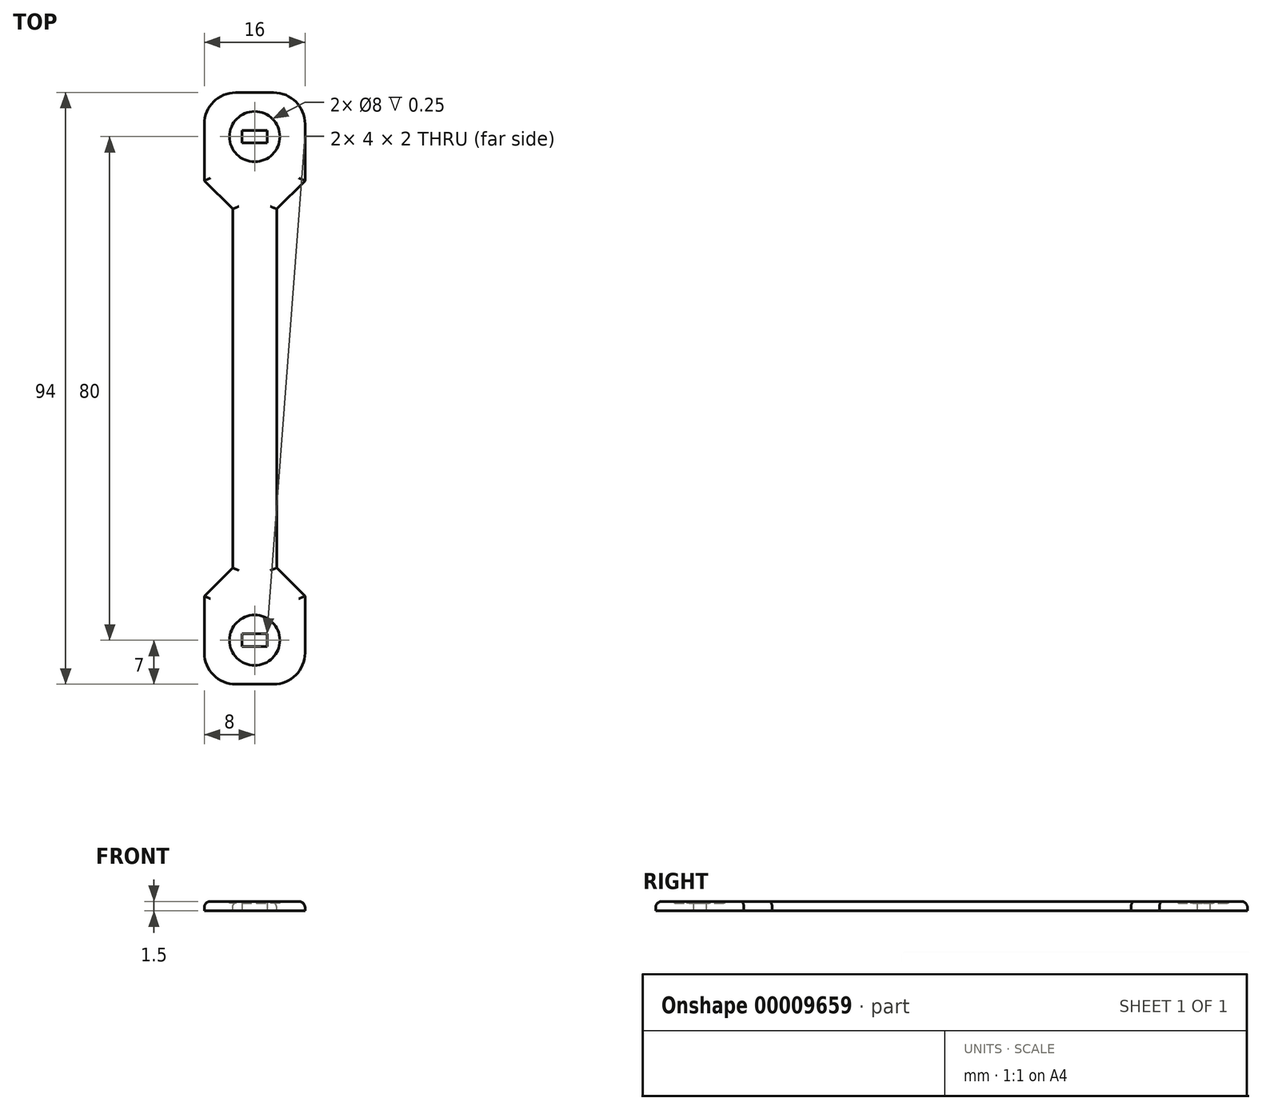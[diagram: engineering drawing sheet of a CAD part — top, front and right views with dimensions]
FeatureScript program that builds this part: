
annotation { "Feature Type Name" : "Feature", "Feature Type Description" : "" }
export const myFeature = defineFeature(function(context is Context, id is Id, definition is map)
    precondition{}
    {
        {
            var Q0;
            Q0=qCreatedBy(makeId("Top.planeOp"),FACE);
            var sketch = newSketch(context, id + "F0", { "sketchPlane" : qUnion([Q0])});
            skCircle(sketch, "E0", {"center": v(0, 40) * mm, "radius": 2 * mm, "construction": true});
            skCircle(sketch, "E1.0.MirrorC", {"center": v(0, -40) * mm, "radius": 2 * mm, "construction": true});
            skLineSegment(sketch, "E2.rect.bottom", {"start": v(-8, 47) * mm, "end": v(8, 47) * mm});
            skLineSegment(sketch, "E2.rect.top", {"start": v(-8, -47) * mm, "end": v(8, -47) * mm});
            skLineSegment(sketch, "E2.rect.left", {"start": v(-8, 47) * mm, "end": v(-8, -47) * mm});
            skLineSegment(sketch, "E2.rect.right", {"start": v(8, 47) * mm, "end": v(8, -47) * mm});
            skPoint(sketch, "E2.rect.middle", {"position": v(0, 0) * mm});
            skLineSegment(sketch, "E3", {"start": v(-8, 33) * mm, "end": v(-3.5, 33) * mm});
            skLineSegment(sketch, "E4", {"start": v(-3.5, 33) * mm, "end": v(-3.5, -33) * mm});
            skLineSegment(sketch, "E5", {"start": v(-8, 0) * mm, "end": v(-3.5, 0) * mm, "construction": true});
            skLineSegment(sketch, "E6.0.MirrorCS", {"start": v(-8, -33) * mm, "end": v(-3.5, -33) * mm});
            skLineSegment(sketch, "E7.0.MirrorCS", {"start": v(8, 33) * mm, "end": v(3.5, 33) * mm});
            skLineSegment(sketch, "E8.0.MirrorCS", {"start": v(3.5, 33) * mm, "end": v(3.5, -33) * mm});
            skLineSegment(sketch, "E9.0.MirrorCS", {"start": v(8, -33) * mm, "end": v(3.5, -33) * mm});
            skLineSegment(sketch, "E10.rect.bottom", {"start": v(-2, -41) * mm, "end": v(2, -41) * mm});
            skLineSegment(sketch, "E10.rect.top", {"start": v(-2, -39) * mm, "end": v(2, -39) * mm});
            skLineSegment(sketch, "E10.rect.left", {"start": v(-2, -41) * mm, "end": v(-2, -39) * mm});
            skLineSegment(sketch, "E10.rect.right", {"start": v(2, -41) * mm, "end": v(2, -39) * mm});
            skLineSegment(sketch, "E11.MirrorCS", {"start": v(-2, 41) * mm, "end": v(-2, 39) * mm});
            skLineSegment(sketch, "E12.MirrorCS", {"start": v(-2, 39) * mm, "end": v(2, 39) * mm});
            skLineSegment(sketch, "E13.MirrorCS", {"start": v(-2, 41) * mm, "end": v(2, 41) * mm});
            skLineSegment(sketch, "E14.MirrorCS", {"start": v(2, 41) * mm, "end": v(2, 39) * mm});
            skSolve(sketch);
        }
        {
            var Q0;
            {var subQ5=sQuery(id+"F0.wireOp",EDGE,"E2.rect.bottom");Q0=makeQuery(id+"F0.imprint","IMPRINT",FACE,{"disambiguationData":[TD([[makeQuery(id+"F0.imprint","IMPRINT",EDGE,{"derivedFrom":subQ5}),-1.0]])]});}
            extrude(context, id + "F1", {"entities" : qUnion([Q0]), "depth" : 1.5 * mm});
        }
        {
            var Q0;
            Q0=makeQuery(id+"F1.opExtrude","SWEPT_EDGE",EDGE,{"disambiguationData":[OSD([sQuery(id+"F0.wireOp",EDGE,"E2.rect.top"),sQuery(id+"F0.wireOp",EDGE,"E2.rect.left")])]});
            var Q1;
            Q1=makeQuery(id+"F1.opExtrude","SWEPT_EDGE",EDGE,{"disambiguationData":[OSD([sQuery(id+"F0.wireOp",EDGE,"E2.rect.top"),sQuery(id+"F0.wireOp",EDGE,"E2.rect.right")])]});
            var Q2;
            Q2=makeQuery(id+"F1.opExtrude","SWEPT_EDGE",EDGE,{"disambiguationData":[OSD([sQuery(id+"F0.wireOp",EDGE,"E2.rect.bottom"),sQuery(id+"F0.wireOp",EDGE,"E2.rect.right")])]});
            var Q3;
            Q3=makeQuery(id+"F1.opExtrude","SWEPT_EDGE",EDGE,{"disambiguationData":[OSD([sQuery(id+"F0.wireOp",EDGE,"E2.rect.bottom"),sQuery(id+"F0.wireOp",EDGE,"E2.rect.left")])]});
            fillet(context, id + "F2", {"entities" : qUnion([Q0, Q1, Q2, Q3]), "radius" : 5 * mm, "tangentPropagation" : true, "allowEdgeOverflow" : false});
        }
        {
            var Q0;
            Q0=makeQuery(id+"F1.opExtrude","SWEPT_EDGE",EDGE,{"disambiguationData":[OSD([sQuery(id+"F0.wireOp",EDGE,"E3"),sQuery(id+"F0.wireOp",EDGE,"E4")])]});
            var Q1;
            Q1=makeQuery(id+"F1.opExtrude","SWEPT_EDGE",EDGE,{"disambiguationData":[OSD([sQuery(id+"F0.wireOp",EDGE,"E7.0.MirrorCS"),sQuery(id+"F0.wireOp",EDGE,"E8.0.MirrorCS")])]});
            var Q2;
            Q2=makeQuery(id+"F1.opExtrude","SWEPT_EDGE",EDGE,{"disambiguationData":[OSD([sQuery(id+"F0.wireOp",EDGE,"E8.0.MirrorCS"),sQuery(id+"F0.wireOp",EDGE,"E9.0.MirrorCS")])]});
            var Q3;
            Q3=makeQuery(id+"F1.opExtrude","SWEPT_EDGE",EDGE,{"disambiguationData":[OSD([sQuery(id+"F0.wireOp",EDGE,"E4"),sQuery(id+"F0.wireOp",EDGE,"E6.0.MirrorCS")])]});
            chamfer(context, id + "F3", {"entities" : qUnion([Q0, Q1, Q2, Q3]), "width" : 4.5 * mm, "tangentPropagation" : true});
        }
        {
            var Q0;
            {var subQ0=sQuery(id+"F0.wireOp",EDGE,"E8.0.MirrorCS");var subQ1=sQuery(id+"F0.wireOp",EDGE,"E9.0.MirrorCS");Q0=makeQuery(id+"F3.opChamfer","BLEND_EDGE",EDGE,{"blendedFrom":[makeQuery(id+"F1.opExtrude","SWEPT_EDGE",EDGE,{"disambiguationData":[OSD([subQ0,subQ1])]}),makeQuery(id+"F1.opExtrude","CAP_FACE",FACE,{"disambiguationData":[OSD([sQuery(id+"F0.wireOp",EDGE,"E0"),sQuery(id+"F0.wireOp",EDGE,"E1.0.MirrorC"),sQuery(id+"F0.wireOp",EDGE,"E2.rect.bottom"),sQuery(id+"F0.wireOp",EDGE,"E2.rect.top"),sQuery(id+"F0.wireOp",EDGE,"E2.rect.left"),sQuery(id+"F0.wireOp",EDGE,"E2.rect.right"),sQuery(id+"F0.wireOp",EDGE,"E3"),sQuery(id+"F0.wireOp",EDGE,"E4"),sQuery(id+"F0.wireOp",EDGE,"E6.0.MirrorCS"),sQuery(id+"F0.wireOp",EDGE,"E7.0.MirrorCS"),subQ0,subQ1])],"isStart":false})],"blendedInto":[makeQuery(id+"F1.opExtrude","CAP_FACE",FACE,{"disambiguationData":[OSD([sQuery(id+"F0.wireOp",EDGE,"E0"),sQuery(id+"F0.wireOp",EDGE,"E1.0.MirrorC"),sQuery(id+"F0.wireOp",EDGE,"E2.rect.bottom"),sQuery(id+"F0.wireOp",EDGE,"E2.rect.top"),sQuery(id+"F0.wireOp",EDGE,"E2.rect.left"),sQuery(id+"F0.wireOp",EDGE,"E2.rect.right"),sQuery(id+"F0.wireOp",EDGE,"E3"),sQuery(id+"F0.wireOp",EDGE,"E4"),sQuery(id+"F0.wireOp",EDGE,"E6.0.MirrorCS"),sQuery(id+"F0.wireOp",EDGE,"E7.0.MirrorCS"),subQ0,subQ1])],"isStart":false})]});}
            var Q1;
            Q1=makeQuery(id+"F1.opExtrude","CAP_EDGE",EDGE,{"disambiguationData":[OSD([sQuery(id+"F0.wireOp",EDGE,"E8.0.MirrorCS")])],"isStart":false});
            var Q2;
            Q2=makeQuery(id+"F1.opExtrude","CAP_EDGE",EDGE,{"disambiguationData":[OSD([sQuery(id+"F0.wireOp",EDGE,"E4")])],"isStart":false});
            var Q3;
            {var subQ0=sQuery(id+"F0.wireOp",EDGE,"E4");var subQ1=sQuery(id+"F0.wireOp",EDGE,"E6.0.MirrorCS");Q3=makeQuery(id+"F3.opChamfer","BLEND_EDGE",EDGE,{"blendedFrom":[makeQuery(id+"F1.opExtrude","SWEPT_EDGE",EDGE,{"disambiguationData":[OSD([subQ0,subQ1])]}),makeQuery(id+"F1.opExtrude","CAP_FACE",FACE,{"disambiguationData":[OSD([sQuery(id+"F0.wireOp",EDGE,"E0"),sQuery(id+"F0.wireOp",EDGE,"E1.0.MirrorC"),sQuery(id+"F0.wireOp",EDGE,"E2.rect.bottom"),sQuery(id+"F0.wireOp",EDGE,"E2.rect.top"),sQuery(id+"F0.wireOp",EDGE,"E2.rect.left"),sQuery(id+"F0.wireOp",EDGE,"E2.rect.right"),sQuery(id+"F0.wireOp",EDGE,"E3"),subQ0,subQ1,sQuery(id+"F0.wireOp",EDGE,"E7.0.MirrorCS"),sQuery(id+"F0.wireOp",EDGE,"E8.0.MirrorCS"),sQuery(id+"F0.wireOp",EDGE,"E9.0.MirrorCS")])],"isStart":false})],"blendedInto":[makeQuery(id+"F1.opExtrude","CAP_FACE",FACE,{"disambiguationData":[OSD([sQuery(id+"F0.wireOp",EDGE,"E0"),sQuery(id+"F0.wireOp",EDGE,"E1.0.MirrorC"),sQuery(id+"F0.wireOp",EDGE,"E2.rect.bottom"),sQuery(id+"F0.wireOp",EDGE,"E2.rect.top"),sQuery(id+"F0.wireOp",EDGE,"E2.rect.left"),sQuery(id+"F0.wireOp",EDGE,"E2.rect.right"),sQuery(id+"F0.wireOp",EDGE,"E3"),subQ0,subQ1,sQuery(id+"F0.wireOp",EDGE,"E7.0.MirrorCS"),sQuery(id+"F0.wireOp",EDGE,"E8.0.MirrorCS"),sQuery(id+"F0.wireOp",EDGE,"E9.0.MirrorCS")])],"isStart":false})]});}
            var Q4;
            {var subQ0=sQuery(id+"F0.wireOp",EDGE,"E2.rect.left");Q4=makeQuery(id+"F1.opExtrude","CAP_EDGE",EDGE,{"disambiguationData":[OSD([subQ0]),TDD([makeQuery(id+"F0.imprint","IMPRINT",EDGE,{"disambiguationData":[TD([[makeQuery(id+"F0.imprint","INTERSECT",VERTEX,{"derivedFrom":[sQuery(id+"F0.wireOp",EDGE,"E2.rect.top"),subQ0]}),1.0]])],"derivedFrom":subQ0})])],"isStart":false});}
            var Q5;
            {var subQ0=sQuery(id+"F0.wireOp",EDGE,"E2.rect.left");Q5=makeQuery(id+"F1.opExtrude","CAP_EDGE",EDGE,{"disambiguationData":[OSD([subQ0]),TDD([makeQuery(id+"F0.imprint","IMPRINT",EDGE,{"disambiguationData":[TD([[makeQuery(id+"F0.imprint","INTERSECT",VERTEX,{"derivedFrom":[sQuery(id+"F0.wireOp",EDGE,"E2.rect.bottom"),subQ0]}),-1.0]])],"derivedFrom":subQ0})])],"isStart":false});}
            var Q6;
            {var subQ0=sQuery(id+"F0.wireOp",EDGE,"E3");var subQ1=sQuery(id+"F0.wireOp",EDGE,"E4");Q6=makeQuery(id+"F3.opChamfer","BLEND_EDGE",EDGE,{"blendedFrom":[makeQuery(id+"F1.opExtrude","SWEPT_EDGE",EDGE,{"disambiguationData":[OSD([subQ0,subQ1])]}),makeQuery(id+"F1.opExtrude","CAP_FACE",FACE,{"disambiguationData":[OSD([sQuery(id+"F0.wireOp",EDGE,"E0"),sQuery(id+"F0.wireOp",EDGE,"E1.0.MirrorC"),sQuery(id+"F0.wireOp",EDGE,"E2.rect.bottom"),sQuery(id+"F0.wireOp",EDGE,"E2.rect.top"),sQuery(id+"F0.wireOp",EDGE,"E2.rect.left"),sQuery(id+"F0.wireOp",EDGE,"E2.rect.right"),subQ0,subQ1,sQuery(id+"F0.wireOp",EDGE,"E6.0.MirrorCS"),sQuery(id+"F0.wireOp",EDGE,"E7.0.MirrorCS"),sQuery(id+"F0.wireOp",EDGE,"E8.0.MirrorCS"),sQuery(id+"F0.wireOp",EDGE,"E9.0.MirrorCS")])],"isStart":false})],"blendedInto":[makeQuery(id+"F1.opExtrude","CAP_FACE",FACE,{"disambiguationData":[OSD([sQuery(id+"F0.wireOp",EDGE,"E0"),sQuery(id+"F0.wireOp",EDGE,"E1.0.MirrorC"),sQuery(id+"F0.wireOp",EDGE,"E2.rect.bottom"),sQuery(id+"F0.wireOp",EDGE,"E2.rect.top"),sQuery(id+"F0.wireOp",EDGE,"E2.rect.left"),sQuery(id+"F0.wireOp",EDGE,"E2.rect.right"),subQ0,subQ1,sQuery(id+"F0.wireOp",EDGE,"E6.0.MirrorCS"),sQuery(id+"F0.wireOp",EDGE,"E7.0.MirrorCS"),sQuery(id+"F0.wireOp",EDGE,"E8.0.MirrorCS"),sQuery(id+"F0.wireOp",EDGE,"E9.0.MirrorCS")])],"isStart":false})]});}
            var Q7;
            {var subQ0=sQuery(id+"F0.wireOp",EDGE,"E7.0.MirrorCS");var subQ1=sQuery(id+"F0.wireOp",EDGE,"E8.0.MirrorCS");Q7=makeQuery(id+"F3.opChamfer","BLEND_EDGE",EDGE,{"blendedFrom":[makeQuery(id+"F1.opExtrude","SWEPT_EDGE",EDGE,{"disambiguationData":[OSD([subQ0,subQ1])]}),makeQuery(id+"F1.opExtrude","CAP_FACE",FACE,{"disambiguationData":[OSD([sQuery(id+"F0.wireOp",EDGE,"E0"),sQuery(id+"F0.wireOp",EDGE,"E1.0.MirrorC"),sQuery(id+"F0.wireOp",EDGE,"E2.rect.bottom"),sQuery(id+"F0.wireOp",EDGE,"E2.rect.top"),sQuery(id+"F0.wireOp",EDGE,"E2.rect.left"),sQuery(id+"F0.wireOp",EDGE,"E2.rect.right"),sQuery(id+"F0.wireOp",EDGE,"E3"),sQuery(id+"F0.wireOp",EDGE,"E4"),sQuery(id+"F0.wireOp",EDGE,"E6.0.MirrorCS"),subQ0,subQ1,sQuery(id+"F0.wireOp",EDGE,"E9.0.MirrorCS")])],"isStart":false})],"blendedInto":[makeQuery(id+"F1.opExtrude","CAP_FACE",FACE,{"disambiguationData":[OSD([sQuery(id+"F0.wireOp",EDGE,"E0"),sQuery(id+"F0.wireOp",EDGE,"E1.0.MirrorC"),sQuery(id+"F0.wireOp",EDGE,"E2.rect.bottom"),sQuery(id+"F0.wireOp",EDGE,"E2.rect.top"),sQuery(id+"F0.wireOp",EDGE,"E2.rect.left"),sQuery(id+"F0.wireOp",EDGE,"E2.rect.right"),sQuery(id+"F0.wireOp",EDGE,"E3"),sQuery(id+"F0.wireOp",EDGE,"E4"),sQuery(id+"F0.wireOp",EDGE,"E6.0.MirrorCS"),subQ0,subQ1,sQuery(id+"F0.wireOp",EDGE,"E9.0.MirrorCS")])],"isStart":false})]});}
            fillet(context, id + "F4", {"entities" : qUnion([Q0, Q1, Q2, Q3, Q4, Q5, Q6, Q7]), "radius" : 1 * mm, "tangentPropagation" : true, "allowEdgeOverflow" : false});
        }
        {
            var Q0;
            Q0=makeQuery(id+"F1.opExtrude","CAP_FACE",FACE,{"disambiguationData":[OSD([sQuery(id+"F0.wireOp",EDGE,"E0"),sQuery(id+"F0.wireOp",EDGE,"E1.0.MirrorC"),sQuery(id+"F0.wireOp",EDGE,"E2.rect.bottom"),sQuery(id+"F0.wireOp",EDGE,"E2.rect.top"),sQuery(id+"F0.wireOp",EDGE,"E2.rect.left"),sQuery(id+"F0.wireOp",EDGE,"E2.rect.right")])],"isStart":false});
            var sketch = newSketch(context, id + "F5", { "sketchPlane" : qUnion([Q0])});
            skCircle(sketch, "E15", {"center": v(0, -40) * mm, "radius": 4 * mm});
            skCircle(sketch, "E16.0.MirrorC", {"center": v(0, 40) * mm, "radius": 4 * mm});
            skLineSegment(sketch, "E17", {"start": v(0, -40) * mm, "end": v(-2, -40) * mm, "construction": true});
            skLineSegment(sketch, "E18", {"start": v(0, -40) * mm, "end": v(0, -41) * mm, "construction": true});
            skSolve(sketch);
        }
        {
            var Q0;
            Q0=qSketchRegion(id+"F5",true);
            extrude(context, id + "F6", {"entities" : qUnion([Q0]), "operationType" : NewBodyOperationType.REMOVE, "oppositeDirection" : true, "depth" : .25 * mm});
        }
    });
